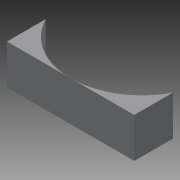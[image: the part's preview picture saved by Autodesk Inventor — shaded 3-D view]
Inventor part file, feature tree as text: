
AUTODESK INVENTOR PART (.ipt)
format: ipt  version: 2013 (Build 170138000, 138)  size: 70,144 bytes
history: native  units: mm
features: other x1, extrude x1, sketch x1
ambient origin geometry x8: Origin, YZ Plane, XZ Plane, XY Plane, X Axis, Y Axis, Z Axis, Center Point
feature tree (3):
  other  "ソリッド1"
  extrude  "押し出し1"  Depth=25.0mm TaperAngle=0.0deg
  sketch  "スケッチ1"
